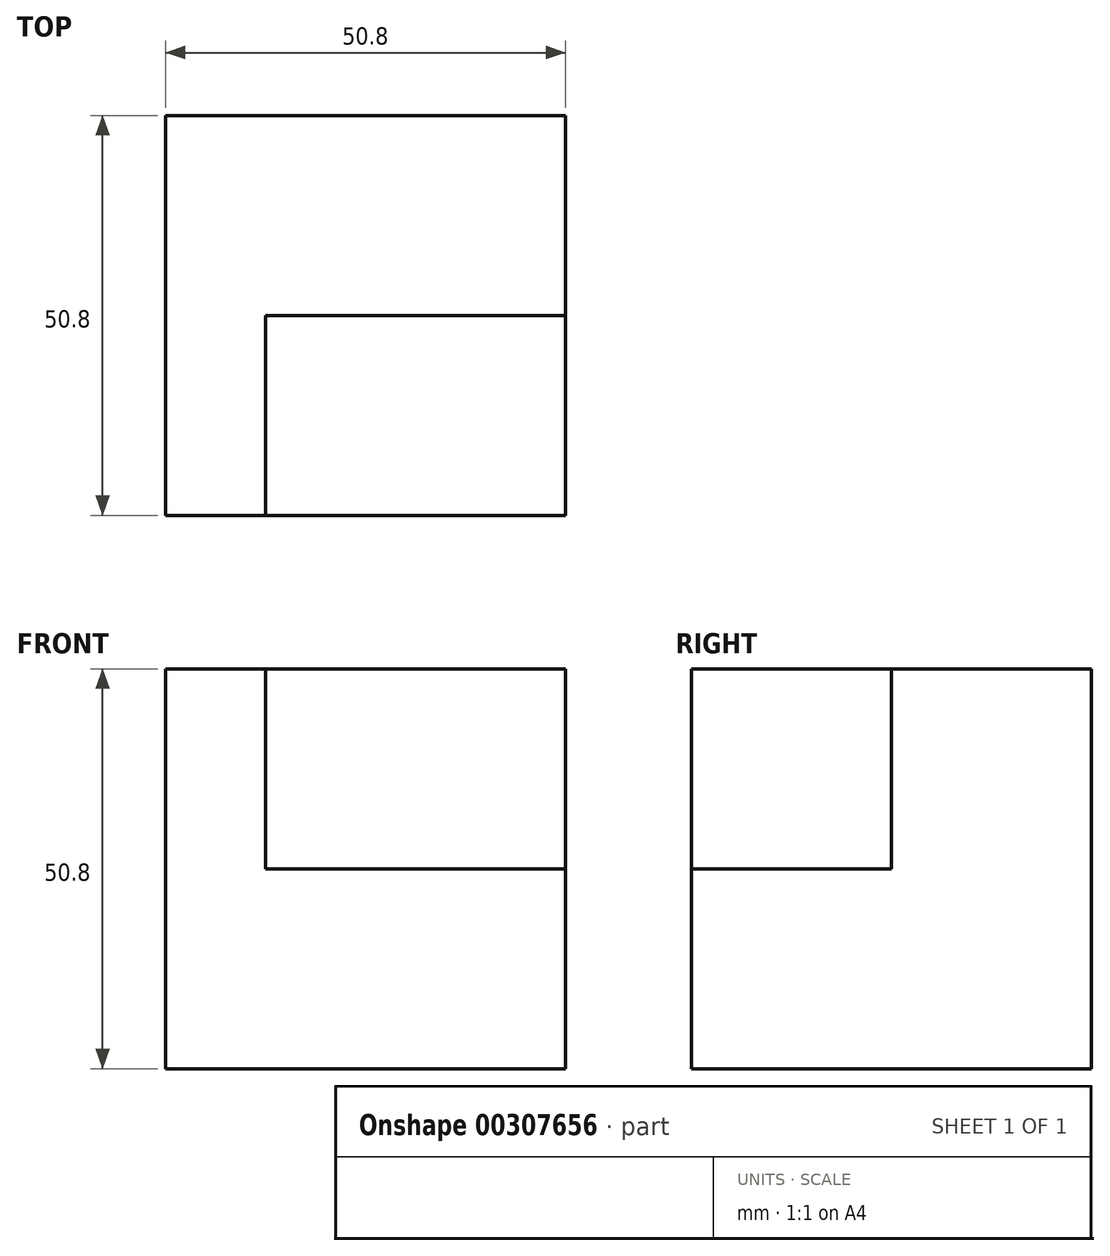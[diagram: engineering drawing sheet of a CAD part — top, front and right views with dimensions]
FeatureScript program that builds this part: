
annotation { "Feature Type Name" : "Feature", "Feature Type Description" : "" }
export const myFeature = defineFeature(function(context is Context, id is Id, definition is map)
    precondition{}
    {
        {
            var Q0;
            Q0=qCreatedBy(makeId("Front.planeOp"),FACE);
            var sketch = newSketch(context, id + "F0", { "sketchPlane" : qUnion([Q0])});
            skLineSegment(sketch, "E0", {"start": v(-23.95, 28.23) * mm, "end": v(26.85, 28.23) * mm});
            skLineSegment(sketch, "E1", {"start": v(26.85, 28.23) * mm, "end": v(26.85, -22.57) * mm});
            skLineSegment(sketch, "E2", {"start": v(26.85, -22.57) * mm, "end": v(-23.95, -22.57) * mm});
            skLineSegment(sketch, "E3", {"start": v(-23.95, -22.57) * mm, "end": v(-23.95, 28.23) * mm});
            skSolve(sketch);
        }
        {
            var Q0;
            Q0 = qSketchRegion(id + "F0", true);
            extrude(context, id + "F1", {"entities" : qUnion([Q0]), "depth" : 50.8 * mm});
        }
        {
            var Q0;
            Q0=makeQuery(id+"F1.opExtrude","CAP_FACE",FACE,{"disambiguationData":[OSD([sQuery(id+"F0.wireOp",EDGE,"E0"),sQuery(id+"F0.wireOp",EDGE,"E1"),sQuery(id+"F0.wireOp",EDGE,"E2"),sQuery(id+"F0.wireOp",EDGE,"E3")])],"isStart":false});
            var sketch = newSketch(context, id + "F2", { "sketchPlane" : qUnion([Q0])});
            skLineSegment(sketch, "E4", {"start": v(-11.25, 28.23) * mm, "end": v(-11.25, 2.83) * mm});
            skLineSegment(sketch, "E5", {"start": v(-11.25, 2.83) * mm, "end": v(26.85, 2.83) * mm});
            skLineSegment(sketch, "E6", {"start": v(26.85, 2.83) * mm, "end": v(26.85, 28.23) * mm});
            skLineSegment(sketch, "E7", {"start": v(26.85, 28.23) * mm, "end": v(-11.25, 28.23) * mm});
            skLineSegment(sketch, "E8", {"start": v(-23.95, 28.23) * mm, "end": v(-11.25, 28.23) * mm});
            skSolve(sketch);
        }
        {
            var Q0;
            Q0 = qSketchRegion(id + "F2", true);
            extrude(context, id + "F3", {"entities" : qUnion([Q0]), "operationType" : NewBodyOperationType.REMOVE, "oppositeDirection" : true, "depth" : 25.4 * mm});
        }
    });
